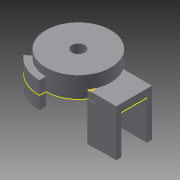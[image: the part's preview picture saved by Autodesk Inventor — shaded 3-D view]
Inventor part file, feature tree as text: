
AUTODESK INVENTOR PART (.ipt)
format: ipt  version: 2013 (Build 170138000, 138)  size: 220,160 bytes
history: native  units: mm
features: sketch x13, extrude x10, other x1, hole x1
ambient origin geometry x8: Origin, YZ Plane, XZ Plane, XY Plane, X Axis, Y Axis, Z Axis, Center Point
feature tree (25):
  other  "ソリッド1"
  extrude  "押し出し1"  Depth=9.768mm
  extrude  "押し出し2"  Depth=15.0mm
  extrude  "押し出し3"  Depth=2.0mm
  extrude  "押し出し4"  Depth=18.0mm
  sketch  "スケッチ5"
  extrude  "押し出し5"  Depth=13.768mm
  extrude  "押し出し6"  Depth=10.0mm TaperAngle=0.0deg
  extrude  "押し出し7"  Depth=2.0mm
  sketch  "スケッチ9"
  extrude  "押し出し8"  Depth=2.0mm
  extrude  "押し出し9"  Depth=12.5mm
  hole  "穴1"  [1 undecoded]
  extrude  "押し出し10"  Depth=30.0mm TaperAngle=0.0deg
  sketch  "スケッチ1"
  sketch  "スケッチ2"
  sketch  "スケッチ3"
  sketch  "スケッチ4"
  sketch  "スケッチ6"
  sketch  "スケッチ7"
  sketch  "スケッチ8"
  sketch  "スケッチ10"
  sketch  "スケッチ11"
  sketch  "スケッチ12"
  sketch  "スケッチ13"
note: 1 required parameter value undecoded (feature->parameter linkage not recoverable at this tier; creation-order binding heuristic only, values carry confidence <= 0.55)
